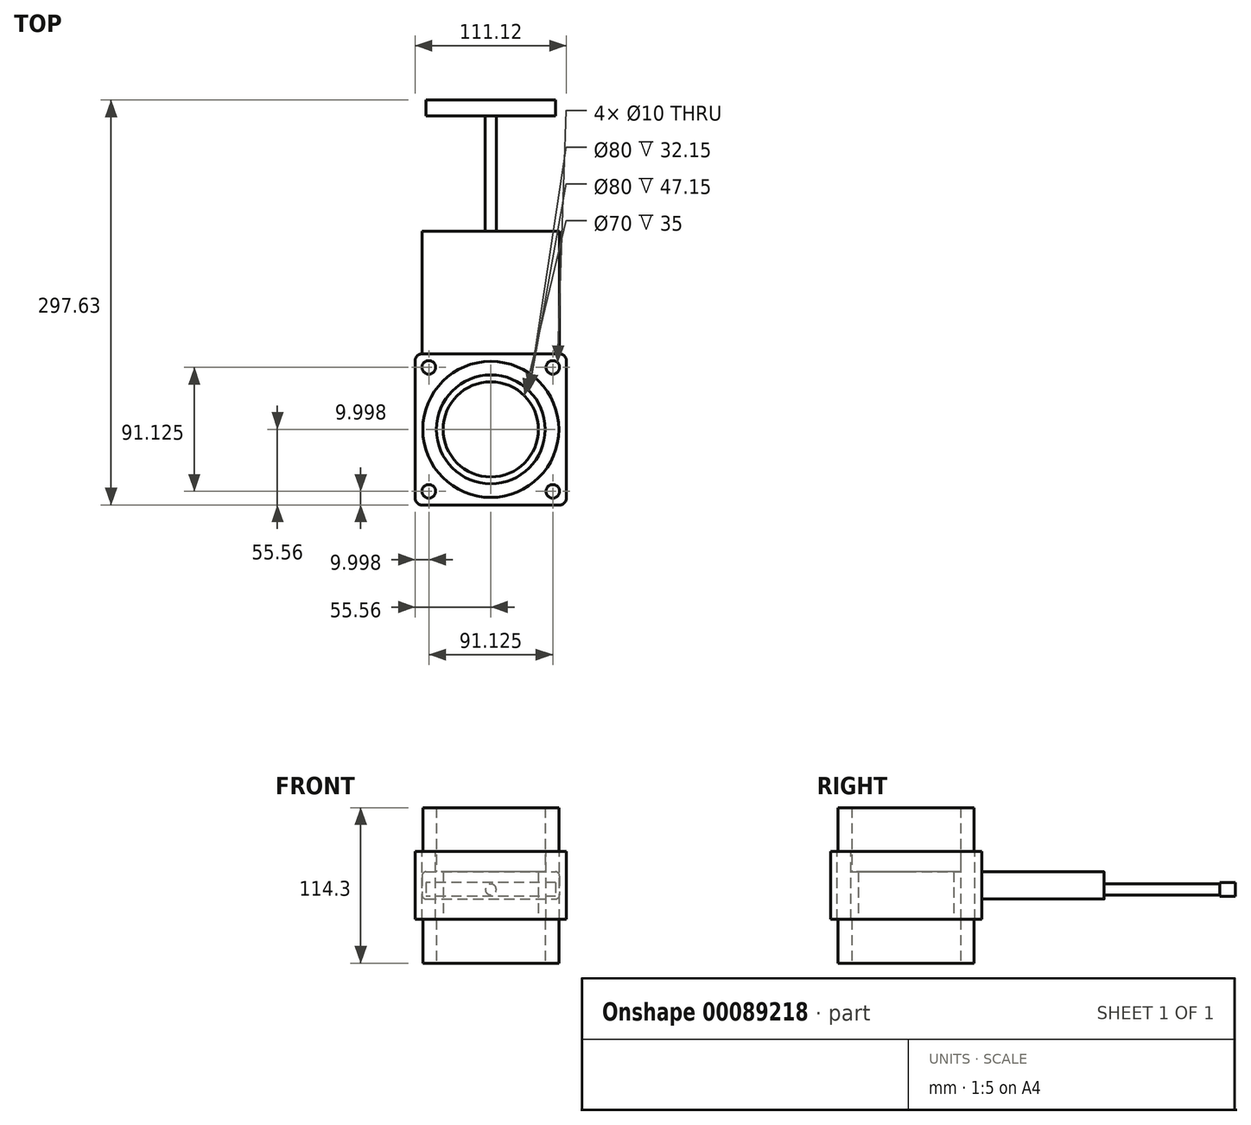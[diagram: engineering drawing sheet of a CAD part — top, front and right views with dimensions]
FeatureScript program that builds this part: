
annotation { "Feature Type Name" : "Feature", "Feature Type Description" : "" }
export const myFeature = defineFeature(function(context is Context, id is Id, definition is map)
    precondition{}
    {
        {
            var Q0;
            Q0=qCreatedBy(makeId("Top.planeOp"),FACE);
            var sketch = newSketch(context, id + "F0", { "sketchPlane" : qUnion([Q0])});
            skCircle(sketch, "E0", {"center": v(0, 0) * mm, "radius": 50 * mm});
            skCircle(sketch, "E1", {"center": v(0, 0) * mm, "radius": 40 * mm});
            skSolve(sketch);
        }
        {
            var Q0;
            Q0=makeQuery(id+"F0.imprint","IMPRINT",FACE,{"disambiguationData":[TD([[makeQuery(id+"F0.imprint","IMPRINT",EDGE,{"derivedFrom":sQuery(id+"F0.wireOp",EDGE,"E0")}),1.0]])]});
            extrude(context, id + "F1", {"entities" : qUnion([Q0]), "depth" : 114.3 * mm});
        }
        {
            var Q0;
            Q0=qCreatedBy(makeId("Top.planeOp"),FACE);
            cPlane(context, id + "F2", {"entities" : qUnion([Q0]), "cplaneType" : CPlaneType.OFFSET, "offset" : 57.15 * mm, "width" : 150 * mm, "height" : 150 * mm});
        }
        {
            var Q0;
            Q0=qCreatedBy(id+"F2.planeOp",FACE);
            var sketch = newSketch(context, id + "F3", { "sketchPlane" : qUnion([Q0])});
            skLineSegment(sketch, "E2.bottom", {"start": v(50.56, 55.56) * mm, "end": v(-50.56, 55.56) * mm});
            skLineSegment(sketch, "E2.top", {"start": v(50.56, -55.56) * mm, "end": v(-50.56, -55.56) * mm});
            skLineSegment(sketch, "E2.left", {"start": v(55.56, 50.56) * mm, "end": v(55.56, -50.56) * mm});
            skLineSegment(sketch, "E2.right", {"start": v(-55.56, 50.56) * mm, "end": v(-55.56, -50.56) * mm});
            skPoint(sketch, "E2.middle", {"position": v(0, 0) * mm});
            skPoint(sketch, "E3.visualSharp", {"position": v(-55.56, 55.56) * mm});
            skArc(sketch, "E3.filletArc", {"start": v(-50.56, 55.56) * mm, "mid": v(-54.1, 54.1) * mm, "end": v(-55.56, 50.56) * mm});
            skPoint(sketch, "E4.visualSharp", {"position": v(55.56, 55.56) * mm});
            skArc(sketch, "E4.filletArc", {"start": v(55.56, 50.56) * mm, "mid": v(54.1, 54.1) * mm, "end": v(50.56, 55.56) * mm});
            skPoint(sketch, "E5.visualSharp", {"position": v(-55.56, -55.56) * mm});
            skArc(sketch, "E5.filletArc", {"start": v(-55.56, -50.56) * mm, "mid": v(-54.1, -54.1) * mm, "end": v(-50.56, -55.56) * mm});
            skPoint(sketch, "E6.visualSharp", {"position": v(55.56, -55.56) * mm});
            skArc(sketch, "E6.filletArc", {"start": v(50.56, -55.56) * mm, "mid": v(54.1, -54.1) * mm, "end": v(55.56, -50.56) * mm});
            skCircle(sketch, "E7", {"center": v(0, 0) * mm, "radius": 50 * mm});
            skSolve(sketch);
        }
        {
            var Q0;
            Q0=makeQuery(id+"F3.imprint","IMPRINT",FACE,{"disambiguationData":[TD([[makeQuery(id+"F3.imprint","IMPRINT",EDGE,{"derivedFrom":sQuery(id+"F3.wireOp",EDGE,"E2.bottom")}),1.0]])]});
            extrude(context, id + "F4", {"entities" : qUnion([Q0]), "operationType" : NewBodyOperationType.ADD, "depth" : 25 * mm, "hasSecondDirection" : true, "secondDirectionOppositeDirection" : true, "secondDirectionDepth" : 25 * mm});
        }
        {
            var Q0;
            Q0=makeQuery(id+"F4.opExtrude","CAP_FACE",FACE,{"disambiguationData":[OSD([sQuery(id+"F3.wireOp",EDGE,"E2.bottom"),sQuery(id+"F3.wireOp",EDGE,"E2.top"),sQuery(id+"F3.wireOp",EDGE,"E2.left"),sQuery(id+"F3.wireOp",EDGE,"E2.right"),sQuery(id+"F3.wireOp",EDGE,"E3.filletArc"),sQuery(id+"F3.wireOp",EDGE,"E4.filletArc"),sQuery(id+"F3.wireOp",EDGE,"E5.filletArc"),sQuery(id+"F3.wireOp",EDGE,"E6.filletArc"),sQuery(id+"F3.wireOp",EDGE,"E7")])],"isStart":false});
            var sketch = newSketch(context, id + "F5", { "sketchPlane" : qUnion([Q0])});
            skCircle(sketch, "E8", {"center": v(-45.56, 45.56) * mm, "radius": 5 * mm});
            skLineSegment(sketch, "E9", {"start": v(-111.13, 111.13) * mm, "end": v(89, -89) * mm, "construction": true});
            skLineSegment(sketch, "E10", {"start": v(-104.03, -104.03) * mm, "end": v(80.23, 80.23) * mm, "construction": true});
            skCircle(sketch, "E11", {"center": v(45.56, 45.56) * mm, "radius": 5 * mm});
            skCircle(sketch, "E12", {"center": v(45.56, -45.56) * mm, "radius": 5 * mm});
            skCircle(sketch, "E13", {"center": v(-45.56, -45.56) * mm, "radius": 5 * mm});
            skSolve(sketch);
        }
        {
            var Q0;
            Q0=makeQuery(id+"F5.imprint","IMPRINT",FACE,{"disambiguationData":[TD([[makeQuery(id+"F5.imprint","IMPRINT",EDGE,{"derivedFrom":sQuery(id+"F5.wireOp",EDGE,"E8")}),1.0]])]});
            var Q1;
            Q1=makeQuery(id+"F5.imprint","IMPRINT",FACE,{"disambiguationData":[TD([[makeQuery(id+"F5.imprint","IMPRINT",EDGE,{"derivedFrom":sQuery(id+"F5.wireOp",EDGE,"E13")}),1.0]])]});
            var Q2;
            Q2=makeQuery(id+"F5.imprint","IMPRINT",FACE,{"disambiguationData":[TD([[makeQuery(id+"F5.imprint","IMPRINT",EDGE,{"derivedFrom":sQuery(id+"F5.wireOp",EDGE,"E12")}),1.0]])]});
            var Q3;
            Q3=makeQuery(id+"F5.imprint","IMPRINT",FACE,{"disambiguationData":[TD([[makeQuery(id+"F5.imprint","IMPRINT",EDGE,{"derivedFrom":sQuery(id+"F5.wireOp",EDGE,"E11")}),1.0]])]});
            extrude(context, id + "F6", {"entities" : qUnion([Q0, Q1, Q2, Q3]), "operationType" : NewBodyOperationType.REMOVE, "endBound" : BoundingType.THROUGH_ALL, "oppositeDirection" : true, "depth" : 25 * mm});
        }
        {
            var Q0;
            Q0=makeQuery(id+"F4.opExtrude","SWEPT_FACE",FACE,{"disambiguationData":[OSD([sQuery(id+"F3.wireOp",EDGE,"E2.bottom")])]});
            var sketch = newSketch(context, id + "F7", { "sketchPlane" : qUnion([Q0])});
            skLineSegment(sketch, "E14.bottom", {"start": v(47.56, 47.15) * mm, "end": v(-47.56, 47.15) * mm});
            skLineSegment(sketch, "E14.top", {"start": v(47.56, 67.15) * mm, "end": v(-47.56, 67.15) * mm});
            skLineSegment(sketch, "E14.left", {"start": v(50.56, 50.15) * mm, "end": v(50.56, 64.15) * mm});
            skLineSegment(sketch, "E14.right", {"start": v(-50.56, 50.15) * mm, "end": v(-50.56, 64.15) * mm});
            skPoint(sketch, "E15.visualSharp", {"position": v(50.56, 47.15) * mm});
            skArc(sketch, "E15.filletArc", {"start": v(47.56, 47.15) * mm, "mid": v(49.68, 48.03) * mm, "end": v(50.56, 50.15) * mm});
            skPoint(sketch, "E16.visualSharp", {"position": v(50.56, 67.15) * mm});
            skArc(sketch, "E16.filletArc", {"start": v(50.56, 64.15) * mm, "mid": v(49.68, 66.27) * mm, "end": v(47.56, 67.15) * mm});
            skPoint(sketch, "E17.visualSharp", {"position": v(-50.56, 67.15) * mm});
            skArc(sketch, "E17.filletArc", {"start": v(-47.56, 67.15) * mm, "mid": v(-49.68, 66.27) * mm, "end": v(-50.56, 64.15) * mm});
            skPoint(sketch, "E18.visualSharp", {"position": v(-50.56, 47.15) * mm});
            skArc(sketch, "E18.filletArc", {"start": v(-50.56, 50.15) * mm, "mid": v(-49.68, 48.03) * mm, "end": v(-47.56, 47.15) * mm});
            skSolve(sketch);
        }
        {
            var Q0;
            Q0 = qSketchRegion(id + "F7", true);
            var Q1;
            Q1=makeQuery(id+"F7.imprint","IMPRINT",FACE,{"disambiguationData":[TD([[makeQuery(id+"F7.imprint","IMPRINT",EDGE,{"derivedFrom":sQuery(id+"F7.wireOp",EDGE,"E14.bottom")}),-1.0]])]});
            extrude(context, id + "F8", {"entities" : qUnion([Q0, Q1]), "operationType" : NewBodyOperationType.ADD, "depth" : 90 * mm});
        }
        {
            var Q0;
            Q0=makeQuery(id+"F8.opExtrude","CAP_FACE",FACE,{"disambiguationData":[OSD([sQuery(id+"F7.wireOp",EDGE,"E14.bottom"),sQuery(id+"F7.wireOp",EDGE,"E14.top"),sQuery(id+"F7.wireOp",EDGE,"E14.left"),sQuery(id+"F7.wireOp",EDGE,"E14.right")])],"isStart":false});
            var sketch = newSketch(context, id + "F9", { "sketchPlane" : qUnion([Q0])});
            skCircle(sketch, "E19", {"center": v(0, 54.15) * mm, "radius": 4 * mm});
            skSolve(sketch);
        }
        {
            var Q0;
            Q0 = qSketchRegion(id + "F9", true);
            extrude(context, id + "F10", {"entities" : qUnion([Q0]), "operationType" : NewBodyOperationType.ADD, "depth" : 85 * mm});
        }
        {
            var Q0;
            Q0=makeQuery(id+"F10.opExtrude","CAP_FACE",FACE,{"disambiguationData":[OSD([sQuery(id+"F9.wireOp",EDGE,"E19")])],"isStart":false});
            var sketch = newSketch(context, id + "F11", { "sketchPlane" : qUnion([Q0])});
            skLineSegment(sketch, "E20.bottom", {"start": v(-47.5, 59.15) * mm, "end": v(47.5, 59.15) * mm});
            skLineSegment(sketch, "E20.top", {"start": v(-47.5, 49.15) * mm, "end": v(47.5, 49.15) * mm});
            skLineSegment(sketch, "E20.left", {"start": v(-47.5, 59.15) * mm, "end": v(-47.5, 49.15) * mm});
            skLineSegment(sketch, "E20.right", {"start": v(47.5, 59.15) * mm, "end": v(47.5, 49.15) * mm});
            skPoint(sketch, "E20.middle", {"position": v(0, 54.15) * mm});
            skSolve(sketch);
        }
        {
            var Q0;
            Q0=makeQuery(id+"F11.imprint","IMPRINT",FACE,{"disambiguationData":[TD([[makeQuery(id+"F11.imprint","IMPRINT",EDGE,{"derivedFrom":makeQuery(id+"F10.opExtrude","CAP_EDGE",EDGE,{"disambiguationData":[OSD([sQuery(id+"F9.wireOp",EDGE,"E19")])],"isStart":false})}),1.0]])]});
            var Q1;
            Q1=makeQuery(id+"F11.imprint","IMPRINT",FACE,{"disambiguationData":[TD([[makeQuery(id+"F11.imprint","IMPRINT",EDGE,{"derivedFrom":sQuery(id+"F11.wireOp",EDGE,"E20.bottom")}),-1.0]])]});
            extrude(context, id + "F12", {"entities" : qUnion([Q0, Q1]), "operationType" : NewBodyOperationType.ADD, "depth" : 11.5 * mm});
        }
        {
            var Q0;
            Q0=qCreatedBy(id+"F2.planeOp",FACE);
            var sketch = newSketch(context, id + "F13", { "sketchPlane" : qUnion([Q0])});
            skCircle(sketch, "E21", {"center": v(0, 0) * mm, "radius": 35 * mm});
            skCircle(sketch, "E22", {"center": v(0, 0) * mm, "radius": 40 * mm});
            skSolve(sketch);
        }
        {
            var Q0;
            Q0=makeQuery(id+"F13.imprint","IMPRINT",FACE,{"disambiguationData":[TD([[makeQuery(id+"F13.imprint","IMPRINT",EDGE,{"derivedFrom":sQuery(id+"F13.wireOp",EDGE,"E21")}),-1.0]])]});
            extrude(context, id + "F14", {"entities" : qUnion([Q0]), "operationType" : NewBodyOperationType.ADD, "depth" : 10 * mm, "hasSecondDirection" : true, "secondDirectionOppositeDirection" : true, "secondDirectionDepth" : 25 * mm});
        }
    });
